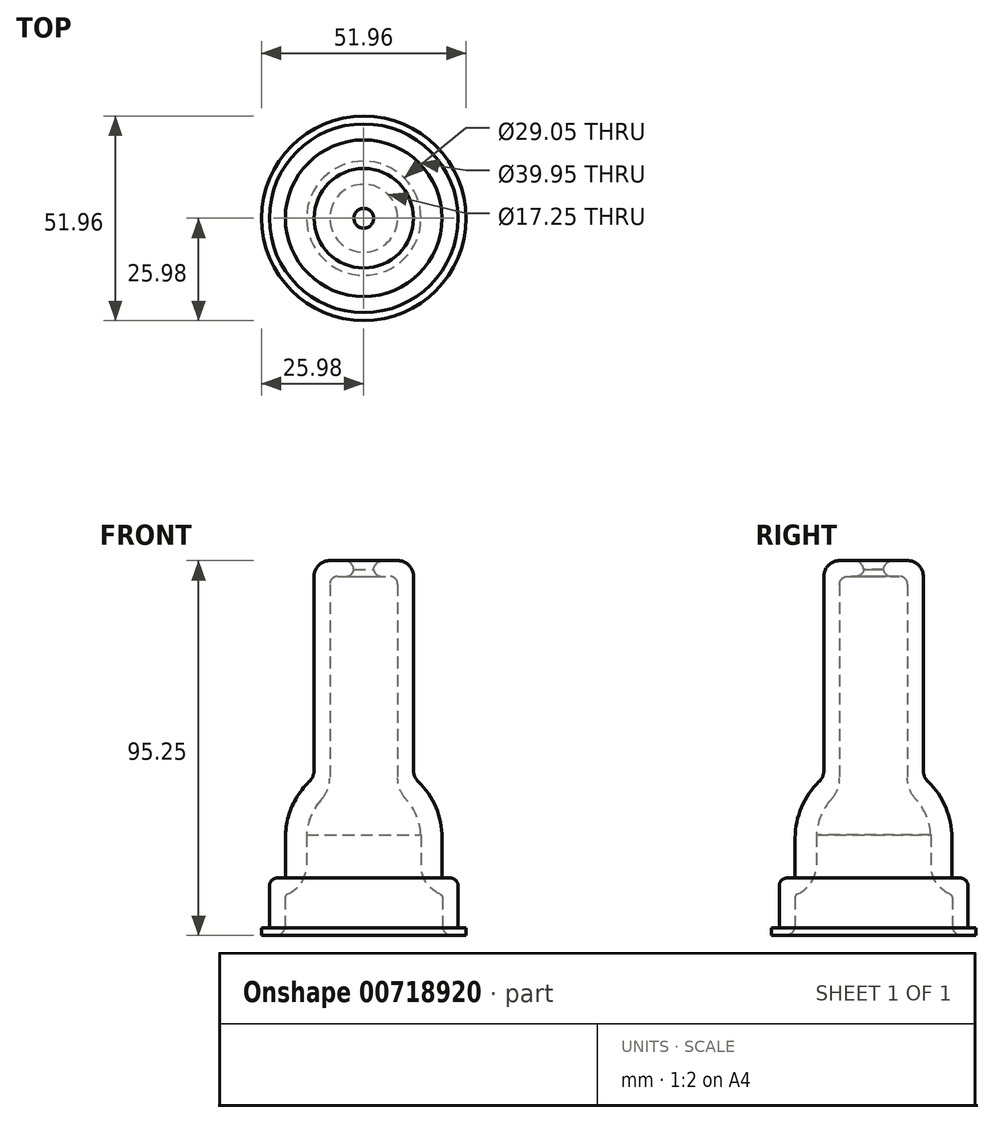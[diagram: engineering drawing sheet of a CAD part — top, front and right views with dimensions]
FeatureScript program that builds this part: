
annotation { "Feature Type Name" : "Feature", "Feature Type Description" : "" }
export const myFeature = defineFeature(function(context is Context, id is Id, definition is map)
    precondition{}
    {
        {
            var Q0;
            Q0=qCreatedBy(makeId("Front.planeOp"),FACE);
            var sketch = newSketch(context, id + "F0", { "sketchPlane" : qUnion([Q0])});
            skLineSegment(sketch, "E0", {"start": v(0, 0) * mm, "end": v(0, 12.2) * mm, "construction": true});
            skLineSegment(sketch, "E1", {"start": v(19.98, 2.5) * mm, "end": v(19.98, 9.6) * mm});
            skLineSegment(sketch, "E2", {"start": v(18.98, 10.6) * mm, "end": v(18.52, 10.6) * mm});
            skLineSegment(sketch, "E3", {"start": v(14.53, 14.6) * mm, "end": v(14.53, 36.5) * mm});
            skLineSegment(sketch, "E4", {"start": v(14.53, 36.5) * mm, "end": v(8.62, 36.5) * mm});
            skLineSegment(sketch, "E5", {"start": v(8.62, 40.02) * mm, "end": v(8.62, 89.25) * mm});
            skLineSegment(sketch, "E6", {"start": v(0, 0) * mm, "end": v(15.93, 0) * mm, "construction": true});
            skLineSegment(sketch, "E7", {"start": v(6.63, 91.25) * mm, "end": v(4.5, 91.25) * mm});
            skLineSegment(sketch, "E8.0", {"start": v(8.63, 95.25) * mm, "end": v(5, 95.25) * mm});
            skLineSegment(sketch, "E8.1", {"start": v(12.63, 41.97) * mm, "end": v(12.63, 91.25) * mm});
            skLineSegment(sketch, "E8.2", {"start": v(23.98, 0) * mm, "end": v(23.98, 12.6) * mm});
            skLineSegment(sketch, "E8.3", {"start": v(21.98, 14.6) * mm, "end": v(19.91, 14.6) * mm});
            skLineSegment(sketch, "E9", {"start": v(2.5, 93.25) * mm, "end": v(2.5, 92.75) * mm});
            skLineSegment(sketch, "E10", {"start": v(19.98, 0) * mm, "end": v(23.98, 0) * mm});
            skPoint(sketch, "E11.visualSharp", {"position": v(8.62, 91.25) * mm});
            skArc(sketch, "E11.filletArc", {"start": v(8.62, 89.25) * mm, "mid": v(8.04, 90.66) * mm, "end": v(6.63, 91.25) * mm});
            skPoint(sketch, "E12.visualSharp", {"position": v(14.53, 10.6) * mm});
            skArc(sketch, "E12.filletArc", {"start": v(14.53, 14.6) * mm, "mid": v(15.7, 11.77) * mm, "end": v(18.52, 10.6) * mm});
            skPoint(sketch, "E13.visualSharp", {"position": v(8.62, 36.5) * mm});
            skPoint(sketch, "E14.visualSharp", {"position": v(19.98, 10.6) * mm});
            skArc(sketch, "E14.filletArc", {"start": v(19.98, 9.6) * mm, "mid": v(19.68, 10.3) * mm, "end": v(18.98, 10.6) * mm});
            skPoint(sketch, "E15.visualSharp", {"position": v(2.5, 91.25) * mm});
            skArc(sketch, "E15.filletArc", {"start": v(2.5, 93.25) * mm, "mid": v(3.09, 91.84) * mm, "end": v(4.5, 91.25) * mm});
            skPoint(sketch, "E16.visualSharp", {"position": v(2.5, 95.25) * mm});
            skArc(sketch, "E16.filletArc", {"start": v(5, 95.25) * mm, "mid": v(3.23, 94.52) * mm, "end": v(2.5, 92.75) * mm});
            skLineSegment(sketch, "E17", {"start": v(22.48, 0) * mm, "end": v(23.98, 0) * mm});
            skPoint(sketch, "E18.visualSharp", {"position": v(19.98, 0) * mm});
            skArc(sketch, "E18.filletArc", {"start": v(19.98, 2.5) * mm, "mid": v(20.7, 0.73) * mm, "end": v(22.48, 0) * mm});
            skPoint(sketch, "E19.visualSharp", {"position": v(12.63, 95.25) * mm});
            skArc(sketch, "E19.filletArc", {"start": v(12.63, 91.25) * mm, "mid": v(11.45, 94.08) * mm, "end": v(8.63, 95.25) * mm});
            skArc(sketch, "E20", {"start": v(14.53, 25.55) * mm, "mid": v(13.41, 30.41) * mm, "end": v(10.73, 34.61) * mm});
            skArc(sketch, "E21.filletArc", {"start": v(8.62, 40.02) * mm, "mid": v(9.17, 37.12) * mm, "end": v(10.73, 34.61) * mm});
            skArc(sketch, "E22", {"start": v(19.91, 24.79) * mm, "mid": v(18.33, 32.56) * mm, "end": v(13.84, 39.1) * mm});
            skLineSegment(sketch, "E23", {"start": v(19.91, 14.6) * mm, "end": v(19.91, 24.79) * mm});
            skPoint(sketch, "E24.visualSharp", {"position": v(12.63, 40.18) * mm});
            skArc(sketch, "E24.filletArc", {"start": v(12.63, 41.97) * mm, "mid": v(12.94, 40.41) * mm, "end": v(13.84, 39.1) * mm});
            skPoint(sketch, "E25.visualSharp", {"position": v(23.98, 14.6) * mm});
            skArc(sketch, "E25.filletArc", {"start": v(23.98, 12.6) * mm, "mid": v(23.39, 14.01) * mm, "end": v(21.98, 14.6) * mm});
            skLineSegment(sketch, "E26.bottom", {"start": v(23.98, 0) * mm, "end": v(25.98, 0) * mm});
            skLineSegment(sketch, "E26.top", {"start": v(23.98, 2) * mm, "end": v(25.98, 2) * mm});
            skLineSegment(sketch, "E26.left", {"start": v(23.98, 0) * mm, "end": v(23.98, 2) * mm});
            skLineSegment(sketch, "E26.right", {"start": v(25.98, 0) * mm, "end": v(25.98, 2) * mm});
            skArc(sketch, "E27", {"start": v(14.53, 17.87) * mm, "mid": v(15.85, 13.47) * mm, "end": v(19.37, 10.52) * mm});
            skLineSegment(sketch, "E28.MirrorCS", {"start": v(-18.98, 10.6) * mm, "end": v(-18.52, 10.6) * mm});
            skLineSegment(sketch, "E29.MirrorCS", {"start": v(-23.98, 0) * mm, "end": v(-23.98, 2) * mm});
            skArc(sketch, "E30.MirrorCS", {"start": v(-19.98, 9.6) * mm, "mid": v(-19.68, 10.3) * mm, "end": v(-18.98, 10.6) * mm});
            skLineSegment(sketch, "E31.MirrorCS", {"start": v(-23.98, 2) * mm, "end": v(-25.98, 2) * mm});
            skLineSegment(sketch, "E32.MirrorCS", {"start": v(-6.63, 91.25) * mm, "end": v(-4.5, 91.25) * mm});
            skLineSegment(sketch, "E33.MirrorCS", {"start": v(-23.98, 0) * mm, "end": v(-25.98, 0) * mm});
            skArc(sketch, "E34.MirrorCS", {"start": v(-5, 95.25) * mm, "mid": v(-3.23, 94.52) * mm, "end": v(-2.5, 92.75) * mm});
            skLineSegment(sketch, "E35.MirrorCS", {"start": v(-2.5, 93.25) * mm, "end": v(-2.5, 92.75) * mm});
            skArc(sketch, "E36.MirrorCS", {"start": v(-2.5, 93.25) * mm, "mid": v(-3.09, 91.84) * mm, "end": v(-4.5, 91.25) * mm});
            skLineSegment(sketch, "E37.MirrorCS", {"start": v(-8.63, 95.25) * mm, "end": v(-5, 95.25) * mm});
            skLineSegment(sketch, "E38.MirrorCS", {"start": v(-22.48, 0) * mm, "end": v(-23.98, 0) * mm});
            skLineSegment(sketch, "E39.MirrorCS", {"start": v(-25.98, 0) * mm, "end": v(-25.98, 2) * mm});
            skArc(sketch, "E40.MirrorCS", {"start": v(-12.63, 41.97) * mm, "mid": v(-12.94, 40.41) * mm, "end": v(-13.84, 39.1) * mm});
            skArc(sketch, "E41.MirrorCS", {"start": v(-19.98, 2.5) * mm, "mid": v(-20.7, 0.73) * mm, "end": v(-22.48, 0) * mm});
            skLineSegment(sketch, "E42.MirrorCS", {"start": v(-19.98, 0) * mm, "end": v(-23.98, 0) * mm});
            skArc(sketch, "E43.MirrorCS", {"start": v(-8.62, 89.25) * mm, "mid": v(-8.04, 90.66) * mm, "end": v(-6.63, 91.25) * mm});
            skLineSegment(sketch, "E44.MirrorCS", {"start": v(-14.52, 36.5) * mm, "end": v(-8.62, 36.5) * mm});
            skArc(sketch, "E45.MirrorCS", {"start": v(-23.98, 12.6) * mm, "mid": v(-23.39, 14.01) * mm, "end": v(-21.98, 14.6) * mm});
            skLineSegment(sketch, "E46.MirrorCS", {"start": v(-19.98, 2.5) * mm, "end": v(-19.98, 9.6) * mm});
            skArc(sketch, "E47.MirrorCS", {"start": v(-8.62, 40.02) * mm, "mid": v(-9.17, 37.12) * mm, "end": v(-10.73, 34.61) * mm});
            skLineSegment(sketch, "E48.MirrorCS", {"start": v(-21.98, 14.6) * mm, "end": v(-19.91, 14.6) * mm});
            skArc(sketch, "E49.MirrorCS", {"start": v(-14.53, 14.6) * mm, "mid": v(-15.7, 11.77) * mm, "end": v(-18.52, 10.6) * mm});
            skArc(sketch, "E50.MirrorCS", {"start": v(-14.53, 17.87) * mm, "mid": v(-15.85, 13.47) * mm, "end": v(-19.37, 10.52) * mm});
            skLineSegment(sketch, "E51.MirrorCS", {"start": v(-19.91, 14.6) * mm, "end": v(-19.91, 24.79) * mm});
            skArc(sketch, "E52.MirrorCS", {"start": v(-12.63, 91.25) * mm, "mid": v(-11.45, 94.08) * mm, "end": v(-8.63, 95.25) * mm});
            skLineSegment(sketch, "E53.MirrorCS", {"start": v(-23.98, 0) * mm, "end": v(-23.98, 12.6) * mm});
            skPoint(sketch, "E54.MirrorP", {"position": v(-8.62, 36.5) * mm});
            skArc(sketch, "E55.MirrorCS", {"start": v(-14.53, 25.55) * mm, "mid": v(-13.41, 30.41) * mm, "end": v(-10.73, 34.61) * mm});
            skPoint(sketch, "E56.MirrorP", {"position": v(-19.98, 10.6) * mm});
            skLineSegment(sketch, "E57.MirrorCS", {"start": v(0, 0) * mm, "end": v(-15.93, 0) * mm, "construction": true});
            skPoint(sketch, "E58.MirrorP", {"position": v(-2.5, 95.25) * mm});
            skLineSegment(sketch, "E59.MirrorCS", {"start": v(-14.53, 14.6) * mm, "end": v(-14.53, 36.5) * mm});
            skPoint(sketch, "E60.MirrorP", {"position": v(-12.63, 40.18) * mm});
            skArc(sketch, "E61.MirrorCS", {"start": v(-19.91, 24.79) * mm, "mid": v(-18.33, 32.56) * mm, "end": v(-13.84, 39.1) * mm});
            skPoint(sketch, "E62.MirrorP", {"position": v(-2.5, 91.25) * mm});
            skPoint(sketch, "E63.MirrorP", {"position": v(-19.98, 0) * mm});
            skPoint(sketch, "E64.MirrorP", {"position": v(-23.98, 14.6) * mm});
            skLineSegment(sketch, "E65.MirrorCS", {"start": v(-8.62, 40.02) * mm, "end": v(-8.62, 89.25) * mm});
            skPoint(sketch, "E66.MirrorP", {"position": v(-12.63, 95.25) * mm});
            skPoint(sketch, "E67.MirrorP", {"position": v(-8.62, 91.25) * mm});
            skLineSegment(sketch, "E68.MirrorCS", {"start": v(-12.63, 41.97) * mm, "end": v(-12.63, 91.25) * mm});
            skPoint(sketch, "E69.MirrorP", {"position": v(-14.53, 10.6) * mm});
            skLineSegment(sketch, "E70", {"start": v(-25.98, 2) * mm, "end": v(-12.63, 95.25) * mm});
            skLineSegment(sketch, "E71", {"start": v(12.63, 95.25) * mm, "end": v(25.98, 2) * mm});
            skLineSegment(sketch, "E72.top", {"start": v(-12.63, 96.75) * mm, "end": v(12.63, 96.75) * mm});
            skLineSegment(sketch, "E72.left", {"start": v(-12.63, 95.25) * mm, "end": v(-12.63, 96.75) * mm});
            skLineSegment(sketch, "E72.right", {"start": v(12.63, 95.25) * mm, "end": v(12.63, 96.75) * mm});
            skLineSegment(sketch, "E73", {"start": v(-5, 92.75) * mm, "end": v(4.5, 93.25) * mm});
            skSolve(sketch);
        }
        {
            var Q0;
            Q0=makeQuery(id+"F0.imprint","IMPRINT",FACE,{"disambiguationData":[TD([[makeQuery(id+"F0.imprint","IMPRINT",EDGE,{"derivedFrom":sQuery(id+"F0.wireOp",EDGE,"E1")}),-1.0]])]});
            var Q1;
            Q1=makeQuery(id+"F0.imprint","IMPRINT",FACE,{"disambiguationData":[TD([[makeQuery(id+"F0.imprint","IMPRINT",EDGE,{"derivedFrom":sQuery(id+"F0.wireOp",EDGE,"E26.bottom")}),1.0]])]});
            var Q2;
            {var subQ3=sQuery(id+"F0.wireOp",EDGE,"E20");Q2=makeQuery(id+"F0.imprint","IMPRINT",FACE,{"disambiguationData":[TD([[makeQuery(id+"F0.imprint","IMPRINT",EDGE,{"derivedFrom":subQ3}),-1.0]])]});}
            var Q3;
            Q3=sQuery(id+"F0.wireOp",EDGE,"E0");
            revolve(context, id + "F1", {"surfaceOperationType" : NewSurfaceOperationType.NEW, "entities" : qUnion([Q0, Q1, Q2]), "axis" : qUnion([Q3]), "revolveType" : RevolveType.FULL});
        }
    });
